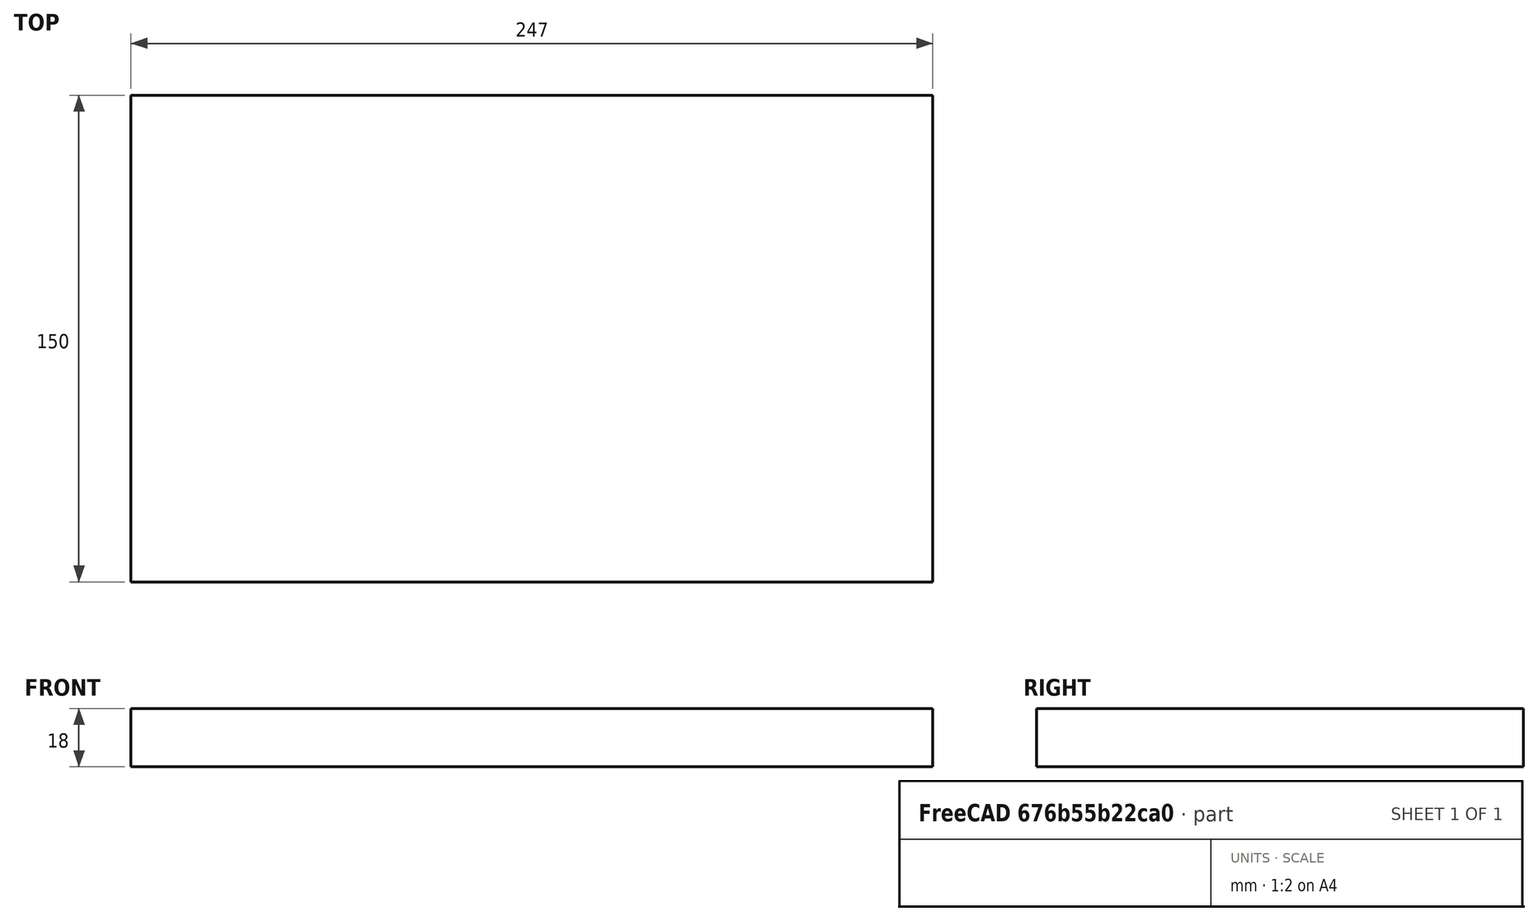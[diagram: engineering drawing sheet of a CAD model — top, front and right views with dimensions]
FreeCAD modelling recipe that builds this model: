
FCSTD DOCUMENT  (FreeCAD 0.18R4 (GitTag))
Label: middle
License: All rights reserved
LicenseURL: http://en.wikipedia.org/wiki/All_rights_reserved
objects: Sketcher::SketchObject×1, PartDesign::Pad×1, PartDesign::Body×1
note: 4 computed .brp shape members not serialized (recipe doc carries the construction recipe); baked Part::Feature solids carry a one-line shape summary decoded from their .brp

FEATURE [Sketcher::SketchObject] Sketch
  MapMode = 5
  Support = -> [XY_Plane]
  sketch-geometry (4):
    g0: LineSegment StartX=0 StartY=0 StartZ=0 EndX=-247 EndY=0 EndZ=0
    g1: LineSegment StartX=-247 StartY=0 StartZ=0 EndX=-247 EndY=150 EndZ=0
    g2: LineSegment StartX=-247 StartY=150 StartZ=0 EndX=0 EndY=150 EndZ=0
    g3: LineSegment StartX=0 StartY=150 StartZ=0 EndX=0 EndY=0 EndZ=0
  constraints (11):
    c: Coincident(g0,g1)
    c: Coincident(g1,g2)
    c: Coincident(g2,g3)
    c: Coincident(g3,g0)
    c: Horizontal(g0)
    c: Horizontal(g2)
    c: Vertical(g1)
    c: Vertical(g3)
    c: Coincident(g0,g-1)
    c: DistanceY(g3,g3) = 150
    c: DistanceX(g2,g2) = 247
FEATURE [PartDesign::Pad] Pad
  Length = 18
  Length2 = 100
  Profile = -> Sketch
  Type = 0
FEATURE [PartDesign::Body] Body
  Group = -> [Sketch,Pad]
  Origin = -> Origin
  Tip = -> Pad
